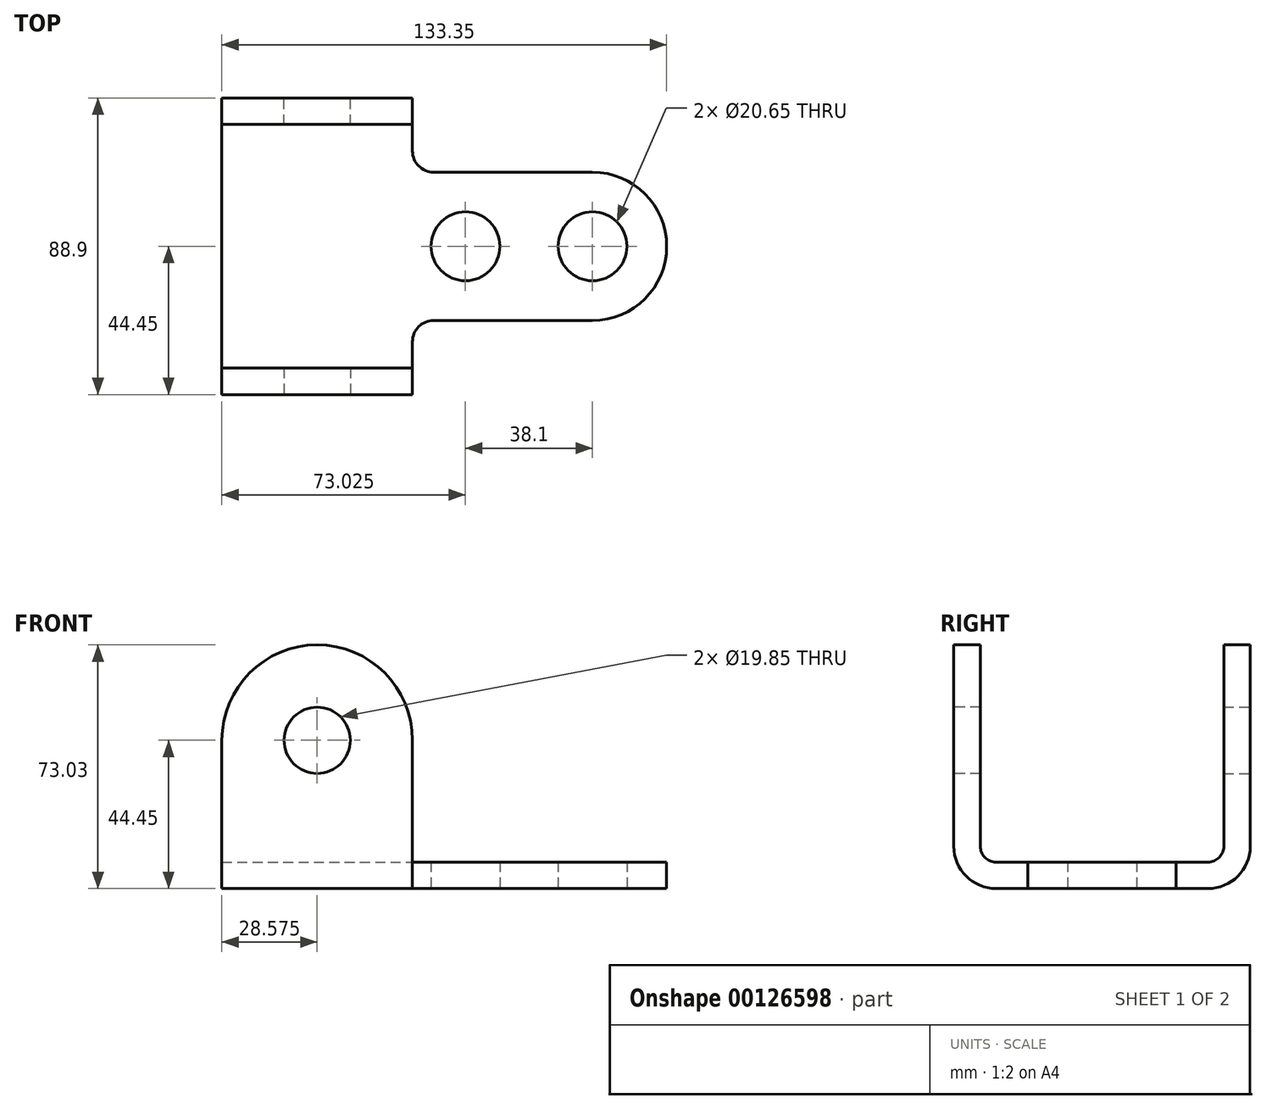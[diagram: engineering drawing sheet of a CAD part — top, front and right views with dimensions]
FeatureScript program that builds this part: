
annotation { "Feature Type Name" : "Feature", "Feature Type Description" : "" }
export const myFeature = defineFeature(function(context is Context, id is Id, definition is map)
    precondition{}
    {
        {
            var Q0;
            Q0=qCreatedBy(makeId("Top.planeOp"),FACE);
            var sketch = newSketch(context, id + "F0", { "sketchPlane" : qUnion([Q0])});
            skLineSegment(sketch, "E0", {"start": v(0, 44.45) * mm, "end": v(0, -44.45) * mm});
            skLineSegment(sketch, "E1", {"start": v(0, 44.45) * mm, "end": v(57.15, 44.45) * mm});
            skLineSegment(sketch, "E2", {"start": v(57.15, 44.45) * mm, "end": v(57.15, 28.57) * mm});
            skLineSegment(sketch, "E3", {"start": v(0, -44.45) * mm, "end": v(57.15, -44.45) * mm});
            skLineSegment(sketch, "E4", {"start": v(57.15, -44.45) * mm, "end": v(57.15, -28.57) * mm});
            skLineSegment(sketch, "E5", {"start": v(63.5, -22.22) * mm, "end": v(111.12, -22.22) * mm});
            skLineSegment(sketch, "E6", {"start": v(63.5, 22.22) * mm, "end": v(111.12, 22.23) * mm});
            skArc(sketch, "E7", {"start": v(111.12, 22.23) * mm, "mid": v(133.35, 0) * mm, "end": v(111.12, -22.23) * mm});
            skPoint(sketch, "E8.visualSharp", {"position": v(57.15, 22.22) * mm});
            skArc(sketch, "E8.filletArc", {"start": v(57.15, 28.57) * mm, "mid": v(59, 24.08) * mm, "end": v(63.5, 22.22) * mm});
            skPoint(sketch, "E9.visualSharp", {"position": v(57.15, -22.22) * mm});
            skArc(sketch, "E9.filletArc", {"start": v(63.5, -22.22) * mm, "mid": v(59, -24.08) * mm, "end": v(57.15, -28.57) * mm});
            skCircle(sketch, "E10", {"center": v(111.12, 0) * mm, "radius": 10.33 * mm});
            skCircle(sketch, "E11", {"center": v(73.03, 0) * mm, "radius": 10.33 * mm});
            skSolve(sketch);
        }
        {
            var Q0;
            Q0 = qSketchRegion(id + "F0", true);
            extrude(context, id + "F1", {"entities" : qUnion([Q0]), "depth" : 7.94 * mm});
        }
        {
            var Q0;
            Q0=makeQuery(id+"F1.opExtrude","SWEPT_FACE",FACE,{"disambiguationData":[OSD([sQuery(id+"F0.wireOp",EDGE,"E3")])]});
            cPlane(context, id + "F2", {"entities" : qUnion([Q0]), "cplaneType" : CPlaneType.OFFSET, "offset" : 0 * mm, "width" : 152.4 * mm, "height" : 152.4 * mm});
        }
        {
            var Q0;
            Q0=qCreatedBy(id+"F2.planeOp",FACE);
            var sketch = newSketch(context, id + "F3", { "sketchPlane" : qUnion([Q0])});
            skLineSegment(sketch, "E12", {"start": v(0, 0) * mm, "end": v(0, 44.45) * mm});
            skLineSegment(sketch, "E13", {"start": v(57.15, 0) * mm, "end": v(57.15, 44.45) * mm});
            skCircle(sketch, "E14", {"center": v(28.58, 44.45) * mm, "radius": 9.92 * mm});
            skArc(sketch, "E15", {"start": v(0, 44.45) * mm, "mid": v(28.58, 73.03) * mm, "end": v(57.15, 44.45) * mm});
            skLineSegment(sketch, "E16", {"start": v(0, 0) * mm, "end": v(57.15, 0) * mm});
            skSolve(sketch);
        }
        {
            var Q0;
            Q0 = qSketchRegion(id + "F3", true);
            extrude(context, id + "F4", {"entities" : qUnion([Q0]), "operationType" : NewBodyOperationType.ADD, "oppositeDirection" : true, "depth" : 7.94 * mm});
        }
        {
            var Q0;
            Q0=makeQuery(id+"F1.opExtrude","SWEPT_FACE",FACE,{"disambiguationData":[OSD([sQuery(id+"F0.wireOp",EDGE,"E1")])]});
            cPlane(context, id + "F5", {"entities" : qUnion([Q0]), "cplaneType" : CPlaneType.OFFSET, "offset" : 0 * mm, "width" : 152.4 * mm, "height" : 152.4 * mm});
        }
        {
            var Q0;
            Q0=qCreatedBy(id+"F5.planeOp",FACE);
            var sketch = newSketch(context, id + "F6", { "sketchPlane" : qUnion([Q0])});
            skLineSegment(sketch, "E17", {"start": v(-57.15, 0) * mm, "end": v(-57.15, 44.45) * mm});
            skLineSegment(sketch, "E18", {"start": v(-57.15, 0) * mm, "end": v(0, 0) * mm});
            skLineSegment(sketch, "E19", {"start": v(0, 0) * mm, "end": v(0, 44.45) * mm});
            skArc(sketch, "E20", {"start": v(-57.15, 44.45) * mm, "mid": v(-28.57, 73.03) * mm, "end": v(0, 44.45) * mm});
            skCircle(sketch, "E21", {"center": v(-28.58, 44.45) * mm, "radius": 9.92 * mm});
            skSolve(sketch);
        }
        {
            var Q0;
            Q0 = qSketchRegion(id + "F6", true);
            extrude(context, id + "F7", {"entities" : qUnion([Q0]), "operationType" : NewBodyOperationType.ADD, "oppositeDirection" : true, "depth" : 7.94 * mm});
        }
        {
            var Q0;
            Q0=makeQuery(id+"F1.opExtrude","CAP_EDGE",EDGE,{"disambiguationData":[OSD([sQuery(id+"F0.wireOp",EDGE,"E1")])],"isStart":true});
            var Q1;
            Q1=makeQuery(id+"F1.opExtrude","CAP_EDGE",EDGE,{"disambiguationData":[OSD([sQuery(id+"F0.wireOp",EDGE,"E3")])],"isStart":true});
            fillet(context, id + "F8", {"entities" : qUnion([Q0, Q1]), "radius" : 12.7 * mm, "tangentPropagation" : true, "allowEdgeOverflow" : false});
        }
        {
            var Q0;
            Q0=makeQuery(id+"F7.boolean.opBoolean","INTERSECT",EDGE,{"derivedFrom":[makeQuery(id+"F1.opExtrude","CAP_FACE",FACE,{"disambiguationData":[OSD([sQuery(id+"F0.wireOp",EDGE,"E0"),sQuery(id+"F0.wireOp",EDGE,"E1"),sQuery(id+"F0.wireOp",EDGE,"E2"),sQuery(id+"F0.wireOp",EDGE,"E3"),sQuery(id+"F0.wireOp",EDGE,"E4"),sQuery(id+"F0.wireOp",EDGE,"E5"),sQuery(id+"F0.wireOp",EDGE,"E6"),sQuery(id+"F0.wireOp",EDGE,"E7"),sQuery(id+"F0.wireOp",EDGE,"E8.filletArc"),sQuery(id+"F0.wireOp",EDGE,"E9.filletArc"),sQuery(id+"F0.wireOp",EDGE,"E10"),sQuery(id+"F0.wireOp",EDGE,"E11")])],"isStart":false}),makeQuery(id+"F7.opExtrude","CAP_FACE",FACE,{"disambiguationData":[OSD([sQuery(id+"F6.wireOp",EDGE,"E17"),sQuery(id+"F6.wireOp",EDGE,"E18"),sQuery(id+"F6.wireOp",EDGE,"E19"),sQuery(id+"F6.wireOp",EDGE,"E20"),sQuery(id+"F6.wireOp",EDGE,"E21")])],"isStart":false})]});
            var Q1;
            Q1=makeQuery(id+"F4.boolean.opBoolean","INTERSECT",EDGE,{"derivedFrom":[makeQuery(id+"F1.opExtrude","CAP_FACE",FACE,{"disambiguationData":[OSD([sQuery(id+"F0.wireOp",EDGE,"E0"),sQuery(id+"F0.wireOp",EDGE,"E1"),sQuery(id+"F0.wireOp",EDGE,"E2"),sQuery(id+"F0.wireOp",EDGE,"E3"),sQuery(id+"F0.wireOp",EDGE,"E4"),sQuery(id+"F0.wireOp",EDGE,"E5"),sQuery(id+"F0.wireOp",EDGE,"E6"),sQuery(id+"F0.wireOp",EDGE,"E7"),sQuery(id+"F0.wireOp",EDGE,"E8.filletArc"),sQuery(id+"F0.wireOp",EDGE,"E9.filletArc"),sQuery(id+"F0.wireOp",EDGE,"E10"),sQuery(id+"F0.wireOp",EDGE,"E11")])],"isStart":false}),makeQuery(id+"F4.opExtrude","CAP_FACE",FACE,{"disambiguationData":[OSD([sQuery(id+"F3.wireOp",EDGE,"E12"),sQuery(id+"F3.wireOp",EDGE,"E13"),sQuery(id+"F3.wireOp",EDGE,"E14"),sQuery(id+"F3.wireOp",EDGE,"E15"),sQuery(id+"F3.wireOp",EDGE,"E16")])],"isStart":false})]});
            fillet(context, id + "F9", {"entities" : qUnion([Q0, Q1]), "radius" : 4.76 * mm, "tangentPropagation" : true, "allowEdgeOverflow" : false});
        }
    });
